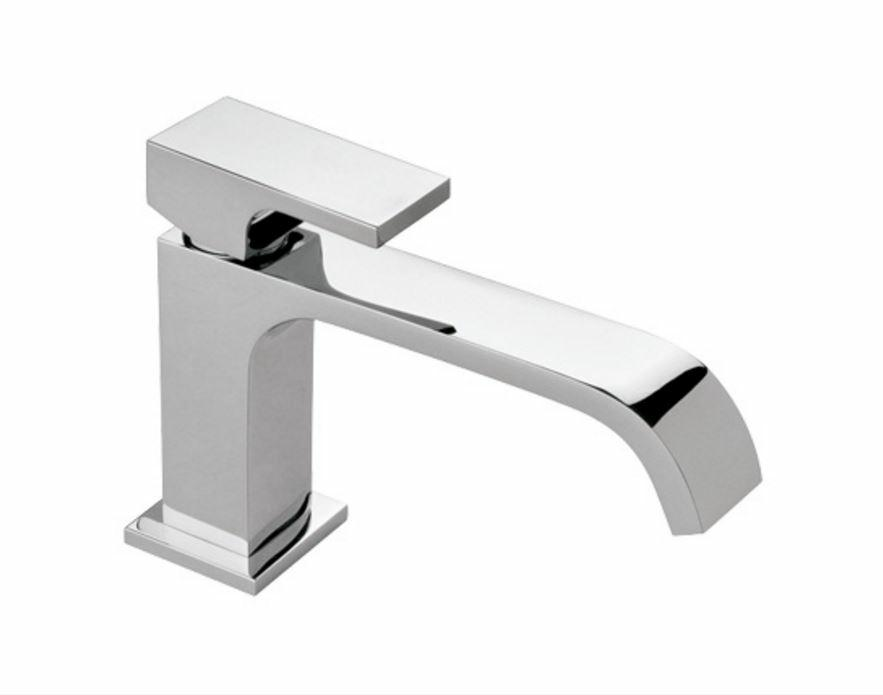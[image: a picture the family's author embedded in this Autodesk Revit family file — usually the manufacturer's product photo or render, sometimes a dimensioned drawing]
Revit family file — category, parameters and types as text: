
# Revit family: Monomando para Lavabo EP-905
name_source: partatom
category: Aparatos sanitarios
revit_build: Autodesk Revit 2016 (Build: 20150220_1215(x64)
units: mm (PartAtom-declared; Revit-internal decimal feet)

## family parameters
Compartido = Sí
Corte con vacíos al cargar = No
Cota de conector redondo = Diámetro de uso
Número OmniClass = 23.45.55.14
Punto de cálculo de habitación = Sí
Se basa en plano de trabajo = Sí
Siempre vertical = Sí
Tipo de pieza = Normal
Título OmniClass = Single Faucets

## types (1)
- EP-905
    Brass Chromed = Brass
    Comentarios de tipo = Single Control Lavatory Faucet
    Data Sheet = http://www.helvex.com.mx
    Descripción = Vértika Single Control With Push Drain Mushroom Drain Without Overflow
    Elevación por defecto = 1"
    Fabricante = HELVEX
    Features = Ceramic Cartridge; Includes Setting Tools; Flexible Hoses 12" Length; Push Drain With Overflow
    Imagen de tipo = EP-905.JPG
    Inlet Threads = ½" - 14 NPSM
    Instructive = http://www.helvex.com.mx
    Max. Working Pressure = 85.3 psi
    Min. Working Pressure = 8.5 psi
    Modelo = EP-905
    Satin = Satín
    Support Base Diameter = 2"
    Total Height = 6"
    Total Length = 8"
    URL = http://www.helvex.com.mx

## geometry (parser evidence)
native form markers: Sweep x3
no freeform markers — native parametric forms only
